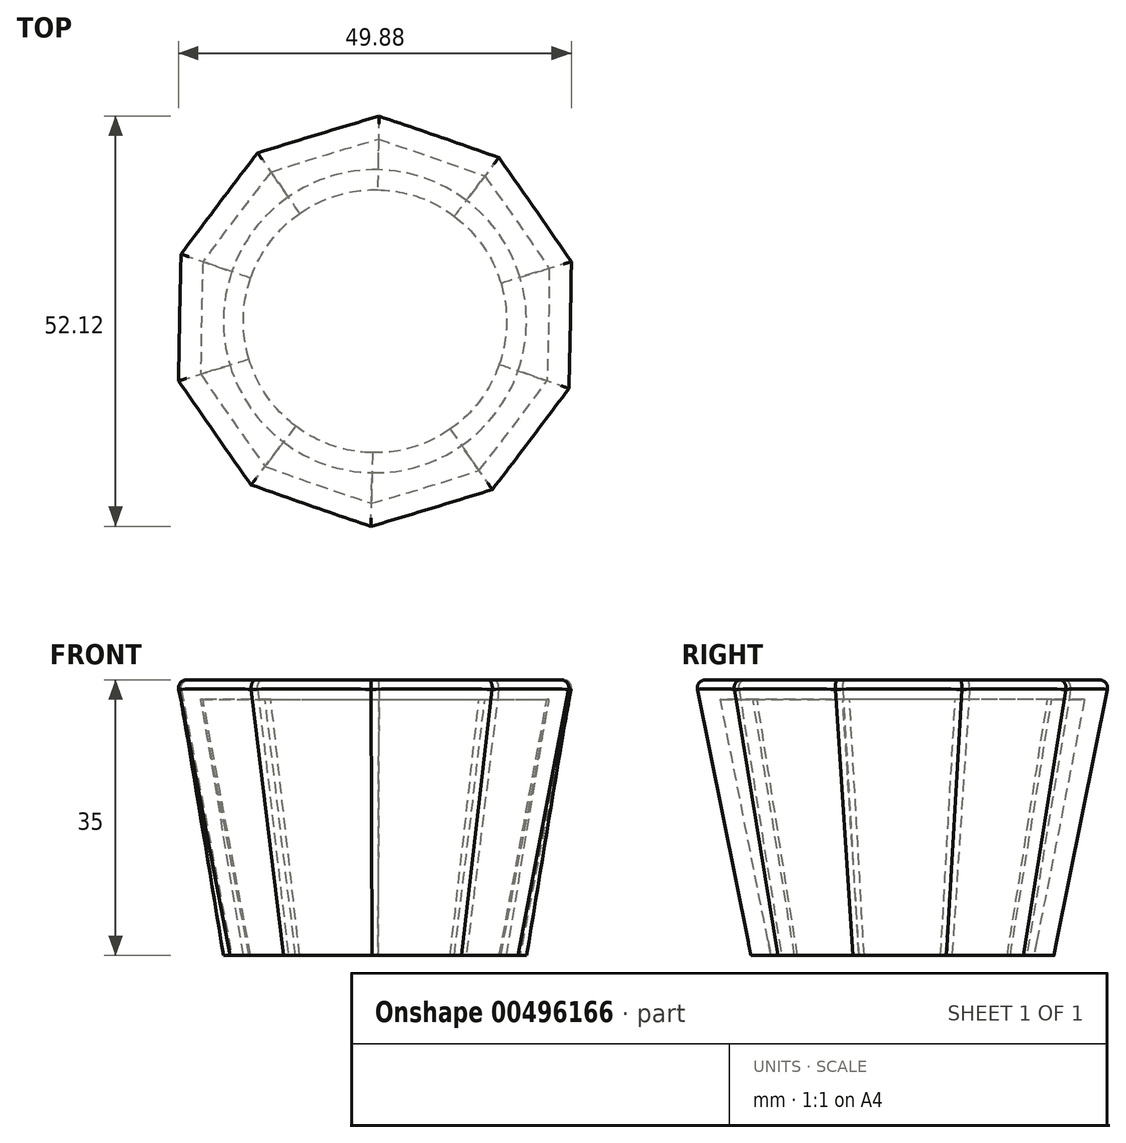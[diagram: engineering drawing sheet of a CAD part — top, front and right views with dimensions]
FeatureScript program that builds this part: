
annotation { "Feature Type Name" : "Feature", "Feature Type Description" : "" }
export const myFeature = defineFeature(function(context is Context, id is Id, definition is map)
    precondition{}
    {
        {
            var Q0;
            Q0=qCreatedBy(makeId("Top.planeOp"),FACE);
            var sketch = newSketch(context, id + "F0", { "sketchPlane" : qUnion([Q0])});
            skCircle(sketch, "E0", {"center": v(0, 0) * mm, "radius": 19.25 * mm});
            skSolve(sketch);
        }
        {
            var Q0;
            Q0=makeQuery(id+"F0.imprint","IMPRINT",FACE,{"disambiguationData":[TD([[makeQuery(id+"F0.imprint","IMPRINT",EDGE,{"derivedFrom":sQuery(id+"F0.wireOp",EDGE,"E0")}),1.0]])]});
            cPlane(context, id + "F1", {"entities" : qUnion([Q0]), "cplaneType" : CPlaneType.OFFSET, "offset" : 35 * mm, "width" : 150 * mm, "height" : 150 * mm});
        }
        {
            var Q0;
            Q0=qCreatedBy(id+"F1.planeOp",FACE);
            var sketch = newSketch(context, id + "F2", { "sketchPlane" : qUnion([Q0])});
            skCircle(sketch, "E1.cCircle", {"center": v(0, 0) * mm, "radius": 25 * mm, "construction": true});
            skLineSegment(sketch, "E1.0", {"start": v(0.51, 26.28) * mm, "end": v(15.86, 20.96) * mm});
            skLineSegment(sketch, "E1.1", {"start": v(15.86, 20.96) * mm, "end": v(25.15, 7.63) * mm});
            skLineSegment(sketch, "E1.2", {"start": v(25.15, 7.63) * mm, "end": v(24.84, -8.6) * mm});
            skLineSegment(sketch, "E1.3", {"start": v(24.84, -8.6) * mm, "end": v(15.03, -21.56) * mm});
            skLineSegment(sketch, "E1.4", {"start": v(15.03, -21.56) * mm, "end": v(-0.51, -26.28) * mm});
            skLineSegment(sketch, "E1.5", {"start": v(-0.51, -26.28) * mm, "end": v(-15.86, -20.96) * mm});
            skLineSegment(sketch, "E1.6", {"start": v(-15.86, -20.96) * mm, "end": v(-25.15, -7.63) * mm});
            skLineSegment(sketch, "E1.7", {"start": v(-25.15, -7.63) * mm, "end": v(-24.84, 8.6) * mm});
            skLineSegment(sketch, "E1.8", {"start": v(-24.84, 8.6) * mm, "end": v(-15.03, 21.56) * mm});
            skLineSegment(sketch, "E1.9", {"start": v(-15.03, 21.56) * mm, "end": v(0.51, 26.28) * mm});
            skPoint(sketch, "E1.0.midPoint", {"position": v(8.19, 23.62) * mm});
            skSolve(sketch);
        }
        {
            var Q0;
            Q0=makeQuery(id+"F2.imprint","IMPRINT",FACE,{"disambiguationData":[TD([[makeQuery(id+"F2.imprint","IMPRINT",EDGE,{"derivedFrom":sQuery(id+"F2.wireOp",EDGE,"E1.0")}),-1.0]])]});
            var Q1;
            Q1=makeQuery(id+"F0.imprint","IMPRINT",FACE,{"disambiguationData":[TD([[makeQuery(id+"F0.imprint","IMPRINT",EDGE,{"derivedFrom":sQuery(id+"F0.wireOp",EDGE,"E0")}),1.0]])]});
            loft(context, id + "F3", {"sheetProfilesArray" : [{ "sheetProfileEntities" : qUnion([Q0]) }, { "sheetProfileEntities" : qUnion([Q1]) }]});
        }
        {
            var Q0;
            Q0=makeQuery(id+"F3.opLoft","CAP_FACE",FACE,{"disambiguationData":[OSD([makeQuery(id+"F2.imprint","IMPRINT",FACE,{"disambiguationData":[TD([[makeQuery(id+"F2.imprint","IMPRINT",EDGE,{"derivedFrom":sQuery(id+"F2.wireOp",EDGE,"E1.0")}),-1.0]])]})])],"isStart":true});
            fillet(context, id + "F4", {"entities" : qUnion([Q0]), "radius" : 1 * mm, "tangentPropagation" : true, "allowEdgeOverflow" : false});
        }
        {
            var Q0;
            Q0=makeQuery(id+"F3.opLoft","CAP_FACE",FACE,{"disambiguationData":[OSD([makeQuery(id+"F0.imprint","IMPRINT",FACE,{"disambiguationData":[TD([[makeQuery(id+"F0.imprint","IMPRINT",EDGE,{"derivedFrom":sQuery(id+"F0.wireOp",EDGE,"E0")}),1.0]])]})])],"isStart":true});
            shell(context, id + "F5", {"entities" : qUnion([Q0]), "thickness" : 2.5 * mm});
        }
    });
